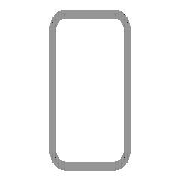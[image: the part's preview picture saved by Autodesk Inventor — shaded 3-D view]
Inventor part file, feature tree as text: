
AUTODESK INVENTOR PART (.ipt)
format: ipt  version: 2025 (Build 290162010, 162A)  size: 134,144 bytes
history: native  units: mm (DEFAULTED — no unit token found)
features: other x4, sketch x1, plane x1
ambient origin geometry x8: Origin, YZ Plane, XZ Plane, XY Plane, X Axis, Y Axis, Z Axis, Center Point
bodies: Solid1 (feature_tree), Body (feature_tree)
feature tree (6):
  parser-record x1  (decoder bookkeeping rows leaked as tree rows — omitted from the tree; the rows remain in map.json)
  other  "Driven Length"
  other  "Start Plane"
  other  "End Plane"
  sketch  "Sketch3"  dims[d3=760.0mm d4=0.0mm d7=4.0mm d9=20.0mm d11=40.0mm d12=2.0mm d13=20.0mm d14=780.0mm d15=10.0mm d16=20.0mm d17=90.0deg d18=760.0mm]
  plane  "Work Plane3"
